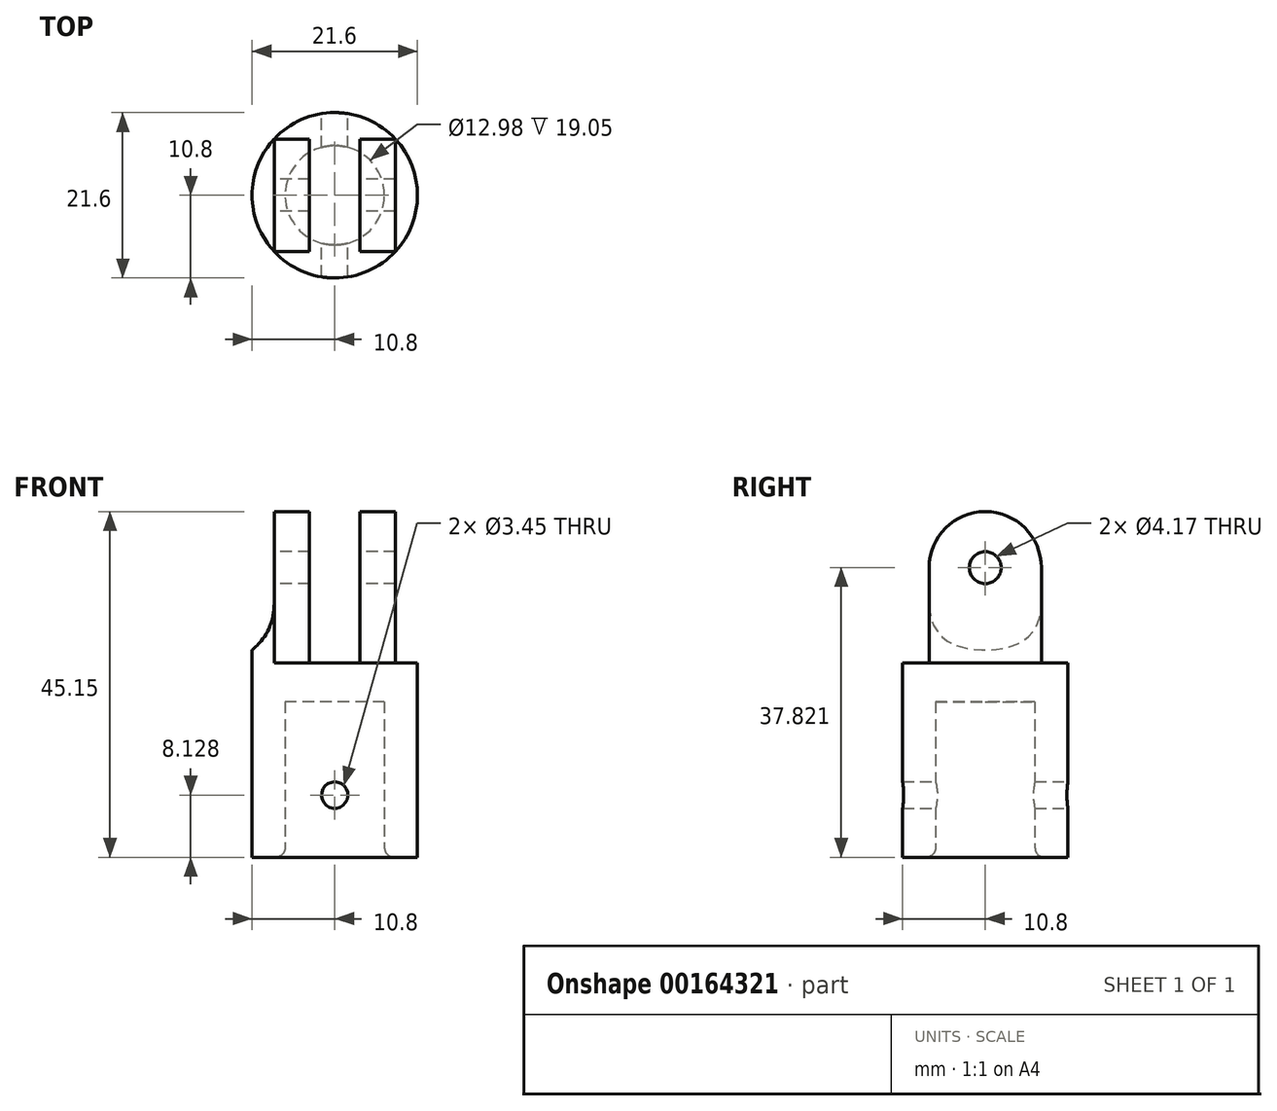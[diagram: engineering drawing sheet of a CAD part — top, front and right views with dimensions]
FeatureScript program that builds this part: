
annotation { "Feature Type Name" : "Feature", "Feature Type Description" : "" }
export const myFeature = defineFeature(function(context is Context, id is Id, definition is map)
    precondition{}
    {
        {
            var Q0;
            Q0=qCreatedBy(makeId("Top.planeOp"),FACE);
            var sketch = newSketch(context, id + "F0", { "sketchPlane" : qUnion([Q0])});
            skCircle(sketch, "E0", {"center": v(0, 0) * mm, "radius": 10.8 * mm});
            skCircle(sketch, "E1", {"center": v(0, 0) * mm, "radius": 6.49 * mm});
            skSolve(sketch);
        }
        {
            var Q0;
            Q0=makeQuery(id+"F0.imprint","IMPRINT",FACE,{"disambiguationData":[TD([[makeQuery(id+"F0.imprint","IMPRINT",EDGE,{"derivedFrom":sQuery(id+"F0.wireOp",EDGE,"E0")}),1.0]])]});
            extrude(context, id + "F1", {"entities" : qUnion([Q0]), "depth" : 20.32 * mm});
        }
        {
            var Q0;
            Q0=makeQuery(id+"F1.opExtrude","CAP_FACE",FACE,{"disambiguationData":[OSD([sQuery(id+"F0.wireOp",EDGE,"E0"),sQuery(id+"F0.wireOp",EDGE,"E1")])],"isStart":false});
            var sketch = newSketch(context, id + "F2", { "sketchPlane" : qUnion([Q0])});
            skCircle(sketch, "E2", {"center": v(0, 0) * mm, "radius": 10.8 * mm});
            skSolve(sketch);
        }
        {
            var Q0;
            Q0 = qSketchRegion(id + "F2", true);
            extrude(context, id + "F3", {"entities" : qUnion([Q0]), "operationType" : NewBodyOperationType.ADD, "depth" : 5.08 * mm});
        }
        {
            var Q0;
            Q0=makeQuery(id+"F3.opExtrude","CAP_FACE",FACE,{"disambiguationData":[OSD([sQuery(id+"F2.wireOp",EDGE,"E2")])],"isStart":false});
            var sketch = newSketch(context, id + "F4", { "sketchPlane" : qUnion([Q0])});
            skLineSegment(sketch, "E3.bottom", {"start": v(-7.92, 7.33) * mm, "end": v(7.92, 7.33) * mm});
            skLineSegment(sketch, "E3.top", {"start": v(-7.92, -7.33) * mm, "end": v(7.92, -7.33) * mm});
            skLineSegment(sketch, "E3.left", {"start": v(-7.92, 7.33) * mm, "end": v(-7.92, -7.33) * mm});
            skLineSegment(sketch, "E3.right", {"start": v(7.92, 7.33) * mm, "end": v(7.92, -7.33) * mm});
            skPoint(sketch, "E3.middle", {"position": v(0, 0) * mm});
            skLineSegment(sketch, "E4.bottom", {"start": v(-3.3, 7.33) * mm, "end": v(3.3, 7.33) * mm});
            skLineSegment(sketch, "E4.top", {"start": v(-3.3, -7.33) * mm, "end": v(3.3, -7.33) * mm});
            skLineSegment(sketch, "E4.left", {"start": v(-3.3, 7.33) * mm, "end": v(-3.3, -7.33) * mm});
            skLineSegment(sketch, "E4.right", {"start": v(3.3, 7.33) * mm, "end": v(3.3, -7.33) * mm});
            skSolve(sketch);
        }
        {
            var Q0;
            {var subQ0=sQuery(id+"F4.wireOp",EDGE,"E3.left");Q0=makeQuery(id+"F4.imprint","IMPRINT",FACE,{"disambiguationData":[TD([[makeQuery(id+"F4.imprint","IMPRINT",EDGE,{"derivedFrom":subQ0}),1.0]])]});}
            var Q1;
            {var subQ0=sQuery(id+"F4.wireOp",EDGE,"E3.right");Q1=makeQuery(id+"F4.imprint","IMPRINT",FACE,{"disambiguationData":[TD([[makeQuery(id+"F4.imprint","IMPRINT",EDGE,{"derivedFrom":subQ0}),-1.0]])]});}
            extrude(context, id + "F5", {"entities" : qUnion([Q0, Q1]), "operationType" : NewBodyOperationType.ADD, "depth" : 12.42 * mm});
        }
        {
            var Q0;
            Q0=qCreatedBy(makeId("Front.planeOp"),FACE);
            var sketch = newSketch(context, id + "F6", { "sketchPlane" : qUnion([Q0])});
            skCircle(sketch, "E5", {"center": v(0, 8.13) * mm, "radius": 1.73 * mm});
            skSolve(sketch);
        }
        {
            var Q0;
            Q0 = qSketchRegion(id + "F6", true);
            extrude(context, id + "F7", {"entities" : qUnion([Q0]), "operationType" : NewBodyOperationType.REMOVE, "endBound" : BoundingType.THROUGH_ALL, "depth" : 25.4 * mm, "hasSecondDirection" : true, "secondDirectionOppositeDirection" : true, "secondDirectionDepth" : 25.4 * mm});
        }
        {
            var Q0;
            Q0=makeQuery(id+"F5.opExtrude","SWEPT_FACE",FACE,{"disambiguationData":[OSD([sQuery(id+"F4.wireOp",EDGE,"E4.right")])]});
            var sketch = newSketch(context, id + "F8", { "sketchPlane" : qUnion([Q0])});
            skCircle(sketch, "E6", {"center": v(0, 37.82) * mm, "radius": 7.33 * mm});
            skSolve(sketch);
        }
        {
            var Q0;
            {var subQ1=sQuery(id+"F4.wireOp",EDGE,"E4.right");var subQ2=makeQuery(id+"F5.opExtrude","CAP_EDGE",EDGE,{"disambiguationData":[OSD([subQ1])],"isStart":false});Q0=makeQuery(id+"F8.imprint","IMPRINT",FACE,{"disambiguationData":[TD([[makeQuery(id+"F8.imprint","IMPRINT",EDGE,{"derivedFrom":subQ2}),1.0]])]});}
            var Q1;
            Q1=makeQuery(id+"F5.opExtrude","SWEPT_FACE",FACE,{"disambiguationData":[OSD([sQuery(id+"F4.wireOp",EDGE,"E3.right")])]});
            extrude(context, id + "F9", {"entities" : qUnion([Q0]), "operationType" : NewBodyOperationType.ADD, "endBound" : BoundingType.UP_TO_SURFACE, "oppositeDirection" : true, "endBoundEntityFace" : qUnion([Q1]), "depth" : 25.4 * mm});
        }
        {
            var Q0;
            Q0=makeQuery(id+"F5.opExtrude","SWEPT_FACE",FACE,{"disambiguationData":[OSD([sQuery(id+"F4.wireOp",EDGE,"E3.left")])]});
            var sketch = newSketch(context, id + "F10", { "sketchPlane" : qUnion([Q0])});
            skCircle(sketch, "E7", {"center": v(0, 37.82) * mm, "radius": 7.33 * mm});
            skSolve(sketch);
        }
        {
            var Q0;
            Q0 = qSketchRegion(id + "F10", true);
            var Q1;
            Q1=makeQuery(id+"F5.opExtrude","SWEPT_FACE",FACE,{"disambiguationData":[OSD([sQuery(id+"F4.wireOp",EDGE,"E4.left")])]});
            extrude(context, id + "F11", {"entities" : qUnion([Q0]), "operationType" : NewBodyOperationType.ADD, "endBound" : BoundingType.UP_TO_SURFACE, "oppositeDirection" : true, "endBoundEntityFace" : qUnion([Q1]), "depth" : 25.4 * mm});
        }
        {
            var Q0;
            Q0=makeQuery(id+"F11.boolean.opBoolean","MERGE",FACE,{"derivedFrom":[makeQuery(id+"F5.opExtrude","SWEPT_FACE",FACE,{"disambiguationData":[OSD([sQuery(id+"F4.wireOp",EDGE,"E3.left")])]}),makeQuery(id+"F11.opExtrude","CAP_FACE",FACE,{"disambiguationData":[OSD([sQuery(id+"F10.wireOp",EDGE,"E7")])],"isStart":true})]});
            var sketch = newSketch(context, id + "F12", { "sketchPlane" : qUnion([Q0])});
            skCircle(sketch, "E8", {"center": v(0, 37.82) * mm, "radius": 2.08 * mm});
            skSolve(sketch);
        }
        {
            var Q0;
            Q0 = qSketchRegion(id + "F12", true);
            extrude(context, id + "F13", {"entities" : qUnion([Q0]), "operationType" : NewBodyOperationType.REMOVE, "endBound" : BoundingType.THROUGH_ALL, "oppositeDirection" : true, "depth" : 25.4 * mm});
        }
        {
            var Q0;
            Q0=makeQuery(id+"F5.opExtrude","CAP_EDGE",EDGE,{"disambiguationData":[OSD([sQuery(id+"F4.wireOp",EDGE,"E3.right")])],"isStart":true});
            var Q1;
            Q1=makeQuery(id+"F5.opExtrude","CAP_EDGE",EDGE,{"disambiguationData":[OSD([sQuery(id+"F4.wireOp",EDGE,"E3.left")])],"isStart":true});
            fillet(context, id + "F14", {"entities" : qUnion([Q0, Q1]), "radius" : 7.62 * mm, "tangentPropagation" : true, "allowEdgeOverflow" : false});
        }
        {
            var Q0;
            Q0=makeQuery(id+"F1.opExtrude","CAP_EDGE",EDGE,{"disambiguationData":[OSD([sQuery(id+"F0.wireOp",EDGE,"E1")])],"isStart":true});
            fillet(context, id + "F15", {"entities" : qUnion([Q0]), "radius" : 1.27 * mm, "tangentPropagation" : true, "allowEdgeOverflow" : false});
        }
    });
